# Revit family: IEK_РозеткаТелевизионная_Встраиваемая_Одноместная_КВАРТА
name_source: partatom
category: Устройства связи
units: mm (PartAtom-declared; Revit-internal decimal feet)

## family parameters
Всегда вертикально = Да
На основе рабочей плоскости = Нет
Общий = Нет
При загрузке вырезать с полостями = Нет
Размер круглого соединителя = Использовать диаметр
Сохранять ориентацию аннотаций = Да
Тип детали = Нормальный
Точка расчета площади = Нет

## types (2) — shared parameters
ADSK_URL страницы изделия = https://www.iek.ru
ADSK_Версия Revit = 2019
ADSK_Версия семейства = 1.00
ADSK_Единица измерения = шт
ADSK_Завод-изготовитель = IEK
ADSK_Марка = КВАРТА
ADSK_Материал наименование = АБС-пластик
IEK_URL = https://www.iek.ru
IEK_Описание = Ассортиментная линейка составлена с учетом тенденций рыночного спроса и включает перечень наиболее актуальных и популярных позиций.
Конструкция шасси позволяет крепить изделие как на винты, так и на распорные лапки в различные типы установочных коробок.
Материал внутреннего механизма - негорючий АБС-пластик.
Шасси розеток и выключателей изготовлены из стали с защитой от коррозии, что обеспечивает надежность и долговечность изделия.
Вся продукция соответствует требованиям действующего российского законодательства в области безопасности продукции (ГОСТ IEC 60884-1 - розетки, ГОСТ Р 51324.1-2005 - выключатели, ГОСТ Р 51324.1-2005, ГОСТ Р 51324.2.1-99 - светорегуляторы).
Образцы новой серии успешно прошли испытания на соответствие требованиям международных стандартов, что подтверждено получением сертификата Таможенного союза, действующего на территории Республики Беларусь, Казахстана и РФ.
IEK_Цена за единицу = 175.56
KSI_CMa_Строительные материалы = 01.7.14.03
Высота = 81 мм
Глубина = 43 мм
Изготовитель = IEK
Тип монтажа = Встраиваемый
Тип соединителя или разъема = TV-SAT
Ширина = 82 мм

## per-type parameters (varying)
| type | ADSK_Код изделия | ADSK_Масса | ADSK_Материал | ADSK_Наименование |
| РТВ10-ККм | EAK10-K33-DM | 0.125 | Цвет кремовый | Розетка 1-местная телевизионная РТВ10-ККм КВАРТА кремовый IEK |
| РТВ10-КБ | EAK10-K01-DM | 0.081 | Цвет белый | Розетка 1-местная телевизионная РТВ10-КБ КВАРТА белый IEK |
